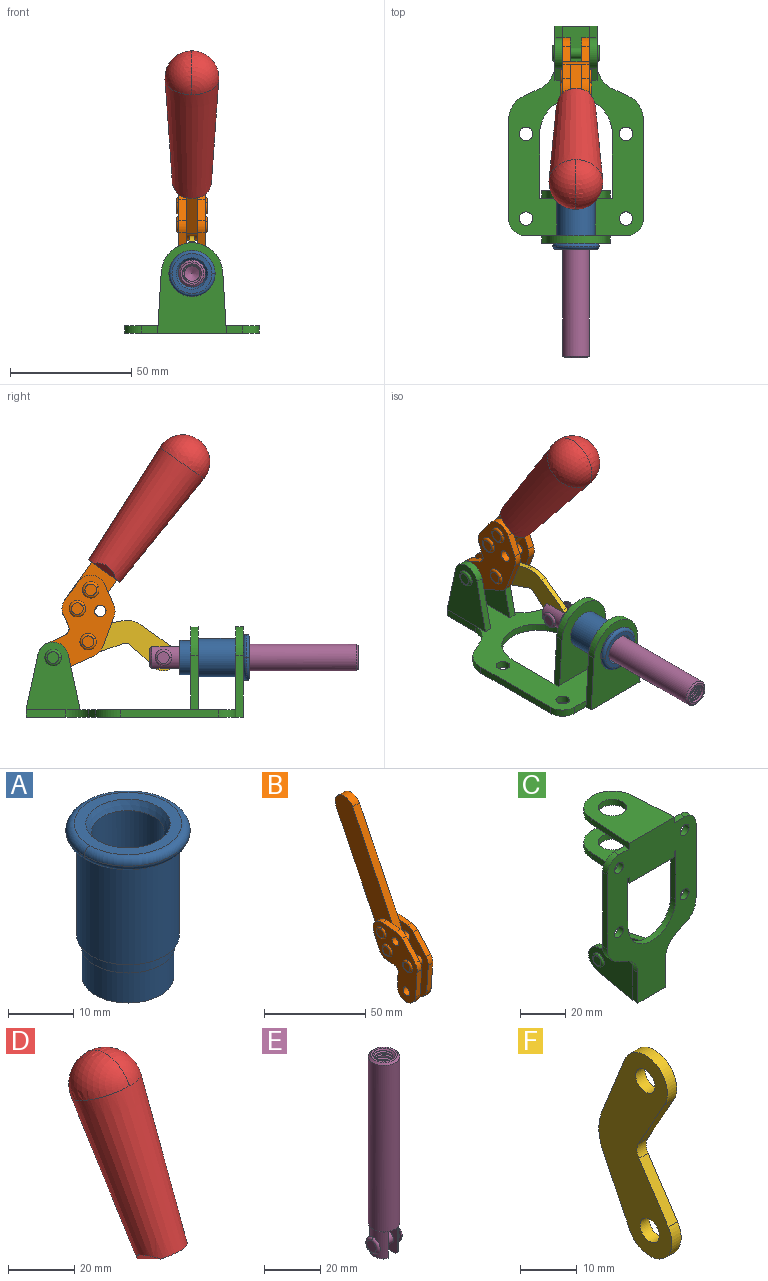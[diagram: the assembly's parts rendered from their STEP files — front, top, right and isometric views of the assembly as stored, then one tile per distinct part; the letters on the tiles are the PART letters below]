
ASSEMBLY  parts=6 mates=6
PART A: 15 faces, bbox 20.6x20.6x28.7 mm
  f0: torus R=8.26mm, axis (0,0,1), area 56.8mm2, adj f1,f10,f12
  f1: torus R=8.26mm, axis (0,0,1), area 56.8mm2, adj f0,f6,f13
  f2: cylinder r=5.59mm len=25.91mm, axis (0,0,1), area 909.6mm2, adj f3,f4
  f3: cone r=6.86mm half-angle=45deg, axis (0,0,-1), area 70.2mm2, adj f2,f14
  f4: cone r=6.47mm half-angle=30deg, axis (0,0,1), area 66.7mm2, adj f2,f13
  f5: cylinder r=7.04mm len=14.07mm, axis (0,0,1), area 252.6mm2, adj f11,f14
  f6: torus R=8.26mm, axis (0,0,1), area 56.8mm2, adj f1,f12,f13
  f7: cylinder r=7.16mm len=14.33mm, axis (0,0,1), area 91.5mm2, adj f9,f11
  f8: cylinder r=7.86mm len=18.42mm, axis (0,0,1), area 909.6mm2, adj f9,f10
  f9: plane 15.72x15.72mm, normal (0,0,-1), area 33mm2, adj f7,f8
  f10: plane 16.51x16.51mm, normal (0,0,-1), area 19.9mm2, adj f0,f8,f12
  f11: plane 14.33x14.33mm, normal (0,0,-1), area 5.7mm2, adj f5,f7
  f12: torus R=8.26mm, axis (0,0,1), area 56.8mm2, adj f0,f6,f10
  f13: plane 16.51x16.51mm, normal (0,0,1), area 82.7mm2, adj f1,f4,f6
  f14: plane 14.07x14.07mm, normal (0,0,-1), area 7.8mm2, adj f3,f5
PART B: 59 faces, bbox 12.9x60.2x99.6 mm
  f0: torus R=2.39mm, axis (-1,0,0), area 14.9mm2, adj f20,f43,f51
  f1: torus R=2.39mm, axis (-1,0,0), area 14.9mm2, adj f19,f42,f51
  f2: torus R=2.39mm, axis (-1,0,0), area 14.9mm2, adj f18,f35,f51
  f3: torus R=2.39mm, axis (-1,0,0), area 14.9mm2, adj f14,f17,f23
  f4: torus R=2.39mm, axis (-1,0,0), area 14.9mm2, adj f13,f16,f23
  f5: torus R=2.39mm, axis (-1,0,0), area 14.9mm2, adj f12,f15,f23
  f6: cylinder r=2.39mm len=4.78mm, axis (1,0,0), area 46.5mm2, adj f48,f50,f51
  f7: cylinder r=2.39mm len=4.78mm, axis (1,0,0), area 46.5mm2, adj f50,f51
  f8: cylinder r=6.35mm len=12.68mm, axis (1,0,0), area 61.8mm2, adj f38,f39,f50,f51
  f9: cylinder r=2.39mm len=4.78mm, axis (-1,0,0), area 70.5mm2, adj f46,f50
  f10: cylinder r=2.39mm len=4.78mm, axis (-1,0,0), area 46.5mm2, adj f23,f45,f46
  f11: cylinder r=2.39mm len=4.78mm, axis (-1,0,0), area 46.5mm2, adj f23,f46
  f12: plane 4.78x4.78mm, normal (1,0,0), area 17.9mm2, adj f5,f15
  f13: plane 4.78x4.78mm, normal (1,0,0), area 17.9mm2, adj f4,f16
  f14: plane 4.78x4.78mm, normal (1,0,0), area 17.9mm2, adj f3,f17
  f15: torus R=2.39mm, axis (-1,0,0), area 14.9mm2, adj f5,f12,f23
  f16: torus R=2.39mm, axis (-1,0,0), area 14.9mm2, adj f4,f13,f23
  f17: torus R=2.39mm, axis (-1,0,0), area 14.9mm2, adj f3,f14,f23
  f18: plane 4.78x4.78mm, normal (-1,0,0), area 17.9mm2, adj f2,f35
  f19: plane 4.78x4.78mm, normal (-1,0,0), area 17.9mm2, adj f1,f42
  f20: plane 4.78x4.78mm, normal (-1,0,0), area 17.9mm2, adj f0,f43
  f21: plane 2.26x0.2mm, normal (1,0,0), area 0.2mm2, adj f31,f44
  f22: plane 2.26x0.2mm, normal (-1,0,0), area 0.2mm2, adj f41,f44
  f23: plane 39.37x30.77mm, normal (1,0,0), area 565.5mm2, adj f3,f4,f5,f10,f11,f15,f16,f17
  f24: cylinder r=6.1mm len=4.15mm, axis (-1,0,0), area 14.7mm2, adj f23,f25,f32,f46
  f25: plane 10.25x9.01mm, normal (0,-0.75,0.66), area 42.3mm2, adj f23,f24,f26,f46
  f26: cylinder r=6.35mm len=4.64mm, axis (-1,0,0), area 15.6mm2, adj f23,f25,f27,f46
  f27: plane 15.84x3.1mm, normal (0,-1,-0.07), area 49.2mm2, adj f23,f26,f28,f46
  f28: cylinder r=6.35mm len=12.68mm, axis (-1,0,0), area 61.8mm2, adj f23,f27,f29,f46
  f29: plane 8.11x3.1mm, normal (0,1,0.07), area 25.2mm2, adj f23,f28,f30,f46
  f30: cylinder r=3.05mm len=3.25mm, axis (-1,0,0), area 14.8mm2, adj f23,f29,f31,f46
  f31: plane 5.99x3.1mm, normal (0,0.07,-1), area 18.6mm2, adj f21,f23,f30,f44,f46
  f32: plane 9.5x3.1mm, normal (0,-0.07,1), area 29.5mm2, adj f23,f24,f33,f46,f47
  f33: cylinder r=6.1mm len=8.63mm, axis (-1,0,0), area 39.1mm2, adj f23,f32,f34,f47
  f34: plane 8.65x3.96mm, normal (0,0.91,-0.42), area 29.5mm2, adj f23,f33,f44,f47
  f35: torus R=2.39mm, axis (-1,0,0), area 14.9mm2, adj f2,f18,f51
  f36: plane 10.25x9.01mm, normal (0,-0.75,0.66), area 42.3mm2, adj f37,f49,f50,f51
  f37: cylinder r=6.35mm len=4.64mm, axis (1,0,0), area 15.6mm2, adj f36,f38,f50,f51
  f38: plane 15.84x3.1mm, normal (0,-1,-0.07), area 49.2mm2, adj f8,f37,f50,f51
  f39: plane 8.11x3.1mm, normal (0,1,0.07), area 25.2mm2, adj f8,f40,f50,f51
  f40: cylinder r=3.05mm len=3.25mm, axis (1,0,0), area 14.8mm2, adj f39,f41,f50,f51
  f41: plane 5.99x3.1mm, normal (0,0.07,-1), area 18.6mm2, adj f22,f40,f44,f50,f51
  f42: torus R=2.39mm, axis (-1,0,0), area 14.9mm2, adj f1,f19,f51
  f43: torus R=2.39mm, axis (-1,0,0), area 14.9mm2, adj f0,f20,f51
  f44: cylinder r=6.35mm len=12.12mm, axis (-1,0,0), area 128.9mm2, adj f21,f22,f23,f31,f34,f41,f46,f47
  f45: plane 2.65x1.35mm, normal (1,0,0), area 1mm2, adj f10,f55
  f46: plane 39.08x20.42mm, normal (-1,0,0), area 412.5mm2, adj f9,f10,f11,f24,f25,f26,f27,f28
  f47: plane 77.62x39.82mm, normal (1,0,0), area 850mm2, adj f32,f33,f34,f44,f53,f54,f55
  f48: plane 2.65x1.35mm, normal (-1,0,0), area 1mm2, adj f6,f55
  f49: cylinder r=6.1mm len=4.15mm, axis (1,0,0), area 14.7mm2, adj f36,f50,f51,f56
  f50: plane 39.08x20.42mm, normal (1,0,0), area 412.5mm2, adj f6,f7,f8,f9,f36,f37,f38,f39
  f51: plane 39.37x30.77mm, normal (-1,0,0), area 565.5mm2, adj f0,f1,f2,f6,f7,f8,f35,f36
  f52: plane 8.65x3.96mm, normal (0,0.91,-0.42), area 29.5mm2, adj f44,f51,f57,f58
  f53: plane 68.49x33.4mm, normal (0,0.9,-0.44), area 358.1mm2, adj f44,f47,f54,f58
  f54: cylinder r=6.35mm len=12.06mm, axis (1,0,0), area 93.7mm2, adj f47,f53,f55,f58
  f55: plane 68.49x33.4mm, normal (0,-0.9,0.44), area 358.1mm2, adj f44,f45,f46,f47,f48,f50,f54,f58
  f56: plane 9.5x3.1mm, normal (0,-0.07,1), area 29.5mm2, adj f49,f50,f51,f57,f58
  f57: cylinder r=6.1mm len=8.63mm, axis (1,0,0), area 39.1mm2, adj f51,f52,f56,f58
  f58: plane 77.62x39.82mm, normal (-1,0,0), area 850mm2, adj f44,f52,f53,f54,f55,f56,f57
PART C: 55 faces, bbox 55.7x37.4x89.8 mm
  f0: torus R=2.41mm, axis (-1,0,0), area 15mm2, adj f11,f15,f25
  f1: torus R=2.41mm, axis (-1,0,0), area 15mm2, adj f10,f12,f22
  f2: cylinder r=2.78mm len=5.56mm, axis (0,-1,0), area 54.2mm2, adj f30,f54
  f3: cylinder r=14.99mm len=29.97mm, axis (0,-1,0), area 145.9mm2, adj f30,f49,f53,f54
  f4: cylinder r=2.78mm len=5.56mm, axis (0,-1,0), area 54.2mm2, adj f30,f54
  f5: cylinder r=2.78mm len=5.56mm, axis (0,-1,0), area 54.2mm2, adj f30,f54
  f6: cylinder r=2.78mm len=5.56mm, axis (0,-1,0), area 54.2mm2, adj f30,f54
  f7: cylinder r=6.35mm len=12.7mm, axis (0,0,1), area 123.6mm2, adj f27,f51
  f8: cylinder r=6.35mm len=12.7mm, axis (0,0,-1), area 124.7mm2, adj f21,f35
  f9: cylinder r=2.41mm len=11.18mm, axis (-1,0,0), area 169.4mm2, adj f16,f19
  f10: plane 4.83x4.83mm, normal (1,0,0), area 18.3mm2, adj f1,f12
  f11: plane 4.83x4.83mm, normal (-1,0,0), area 18.3mm2, adj f0,f15
  f12: torus R=2.41mm, axis (-1,0,0), area 15mm2, adj f1,f10,f22
  f13: cylinder r=6.35mm len=12.41mm, axis (1,0,0), area 53.4mm2, adj f18,f19,f22,f23
  f14: cylinder r=6.35mm len=12.41mm, axis (-1,0,0), area 53.4mm2, adj f16,f17,f24,f25
  f15: torus R=2.41mm, axis (-1,0,0), area 15mm2, adj f0,f11,f25
  f16: plane 27.86x22.35mm, normal (1,0,0), area 425.4mm2, adj f9,f14,f17,f24,f30
  f17: plane 22.86x4.97mm, normal (0,0.21,0.98), area 72.5mm2, adj f14,f16,f25,f30
  f18: plane 22.86x4.97mm, normal (0,0.21,0.98), area 72.5mm2, adj f13,f19,f22,f30
  f19: plane 27.86x22.35mm, normal (-1,0,0), area 425.4mm2, adj f9,f13,f18,f23,f30
  f20: cylinder r=12.7mm len=25.35mm, axis (0,0,-1), area 119.8mm2, adj f21,f34,f35,f36
  f21: plane 34.21x28.07mm, normal (0,0,-1), area 702.4mm2, adj f8,f20,f30,f34,f36
  f22: plane 27.96x22.45mm, normal (1,0,0), area 407.2mm2, adj f1,f12,f13,f18,f23,f30,f42,f43
  f23: plane 22.86x4.97mm, normal (0,0.21,-0.98), area 72.5mm2, adj f13,f19,f22,f44
  f24: plane 22.86x4.97mm, normal (0,0.21,-0.98), area 72.5mm2, adj f14,f16,f25,f44
  f25: plane 27.86x22.35mm, normal (-1,0,0), area 407.1mm2, adj f0,f14,f15,f17,f24,f30,f45,f46
  f26: plane 3.1x0.95mm, normal (0,0,-1), area 2.7mm2, adj f30,f49,f50,f54
  f27: plane 34.21x28.07mm, normal (0,0,1), area 702.4mm2, adj f7,f28,f30,f50,f52
  f28: cylinder r=12.7mm len=25.35mm, axis (0,0,1), area 118.8mm2, adj f27,f50,f51,f52
  f29: plane 3.1x0.95mm, normal (0,0,-1), area 2.7mm2, adj f30,f52,f53,f54
  f30: plane 86.54x55.63mm, normal (0,1,0), area 2362.9mm2, adj f2,f3,f4,f5,f6,f16,f17,f18
  f31: plane 40.56x3.1mm, normal (-1,0,0), area 125.7mm2, adj f30,f32,f48,f54
  f32: cylinder r=7.11mm len=7.11mm, axis (0,-1,0), area 34.6mm2, adj f30,f31,f33,f54
  f33: plane 6.67x3.1mm, normal (0,0,1), area 20.4mm2, adj f30,f32,f34,f54
  f34: plane 25.39x3.13mm, normal (-1,0.06,0), area 79.5mm2, adj f20,f21,f33,f35,f54
  f35: plane 37.31x28.45mm, normal (0,0,1), area 789.9mm2, adj f8,f20,f34,f36,f54
  f36: plane 25.39x3.13mm, normal (1,0.06,0), area 79.5mm2, adj f20,f21,f35,f37,f54
  f37: plane 6.67x3.1mm, normal (0,0,1), area 20.4mm2, adj f30,f36,f38,f54
  f38: cylinder r=7.11mm len=7.11mm, axis (0,-1,0), area 34.6mm2, adj f30,f37,f39,f54
  f39: plane 40.56x3.1mm, normal (1,0,0), area 125.7mm2, adj f30,f38,f40,f54
  f40: cylinder r=11.18mm len=10.16mm, axis (0,-1,0), area 39.5mm2, adj f30,f39,f41,f54
  f41: plane 6.09x3.1mm, normal (0.42,0,-0.91), area 20.8mm2, adj f30,f40,f42,f54
  f42: cylinder r=11.18mm len=9.41mm, axis (0,-1,0), area 37.2mm2, adj f22,f30,f41,f43,f54
  f43: plane 16.5x3.1mm, normal (1,0,0), area 51.1mm2, adj f22,f42,f44,f54
  f44: plane 17.37x3.1mm, normal (0,0,-1), area 53.8mm2, adj f23,f24,f30,f43,f45,f54
  f45: plane 16.5x3.1mm, normal (-1,0,0), area 51.1mm2, adj f25,f44,f46,f54
  f46: cylinder r=11.18mm len=9.41mm, axis (0,-1,0), area 37.2mm2, adj f25,f30,f45,f47,f54
  f47: plane 6.09x3.1mm, normal (-0.42,0,-0.91), area 20.8mm2, adj f30,f46,f48,f54
  f48: cylinder r=11.18mm len=10.16mm, axis (0,-1,0), area 39.5mm2, adj f30,f31,f47,f54
  f49: plane 26.54x3.1mm, normal (-1,0,0), area 82.3mm2, adj f3,f26,f30,f54
  f50: plane 25.39x3.1mm, normal (1,0.06,0), area 78.8mm2, adj f26,f27,f28,f51,f54
  f51: plane 37.31x28.45mm, normal (0,0,-1), area 789.9mm2, adj f7,f28,f50,f52,f54
  f52: plane 25.39x3.1mm, normal (-1,0.06,0), area 78.8mm2, adj f27,f28,f29,f51,f54
  f53: plane 26.54x3.1mm, normal (1,0,0), area 82.3mm2, adj f3,f29,f30,f54
  f54: plane 89.66x55.63mm, normal (0,-1,0), area 2678.5mm2, adj f2,f3,f4,f5,f6,f26,f29,f31
PART D: 11 faces, bbox 22.3x42.6x64.5 mm
  f0: sphere r=11.13mm, area 411.4mm2, adj f1,f8
  f1: cone r=11.11mm half-angle=3.3deg, axis (0,0.44,0.9), area 3251.8mm2, adj f0,f7,f8,f9,f10
  f2: cylinder r=6.16mm len=11.7mm, axis (1,0,0), area 89.5mm2, adj f3,f4,f5,f6
  f3: plane 60.23x36.75mm, normal (-1,0,0), area 763.6mm2, adj f2,f4,f6,f10
  f4: plane 51.37x25.05mm, normal (0,0.9,-0.44), area 264.2mm2, adj f2,f3,f5,f10
  f5: plane 60.23x36.75mm, normal (1,0,0), area 763.6mm2, adj f2,f4,f6,f10
  f6: plane 51.37x25.05mm, normal (0,-0.9,0.44), area 264.2mm2, adj f2,f3,f5,f10
  f7: plane 9.95x5.95mm, normal (0.71,-0.31,-0.64), area 25.8mm2, adj f1,f10
  f8: sphere r=11.13mm, area 411.4mm2, adj f0,f1
  f9: plane 9.95x5.95mm, normal (-0.71,-0.31,-0.64), area 25.8mm2, adj f1,f10
  f10: plane 14.27x11.38mm, normal (0,-0.44,-0.9), area 106.7mm2, adj f1,f3,f4,f5,f6,f7,f9
PART E: 48 faces, bbox 12.6x11.1x86.1 mm
  f0: torus R=2.41mm, axis (-1,0,0), area 15mm2, adj f30,f32,f34
  f1: torus R=2.41mm, axis (-1,0,0), area 15mm2, adj f29,f31,f33
  f2: cylinder r=5.54mm len=72.39mm, axis (0,0,1), area 2518.5mm2, adj f3,f4,f42,f43
  f3: cone r=5.54mm half-angle=45deg, axis (0,0,1), area 7.6mm2, adj f2,f5,f41
  f4: cone r=5.54mm half-angle=45deg, axis (0,0,-1), area 34.9mm2, adj f2,f39
  f5: cylinder r=5.08mm len=11.48mm, axis (0,0,1), area 108.3mm2, adj f3,f7,f8,f41
  f6: cylinder r=2.41mm len=4.83mm, axis (-1,0,0), area 71.2mm2, adj f40,f41
  f7: cylinder r=2.41mm len=4.83mm, axis (-1,0,0), area 7.6mm2, adj f5,f34
  f8: cone r=5.08mm half-angle=45deg, axis (0,0,1), area 10.6mm2, adj f5,f37,f41
  f9: cone r=3.98mm half-angle=45deg, axis (0,0,1), area 17.6mm2, adj f27,f39,f45,f46,f47
  f10: cylinder r=2.41mm len=4.83mm, axis (-1,0,0), area 7.6mm2, adj f33,f38
  f11: cylinder r=3.2mm len=6.4mm, axis (0,0,1), area 78.4mm2, adj f12,f28,f44,f45,f47
  f12: cylinder r=3.2mm len=6.4mm, axis (0,0,1), area 10.5mm2, adj f11,f13,f45,f47
  f13: cylinder r=3.2mm len=6.4mm, axis (0,0,1), area 10.5mm2, adj f12,f14,f45,f47
  f14: cylinder r=3.2mm len=6.4mm, axis (0,0,1), area 10.5mm2, adj f13,f15,f45,f47
  f15: cylinder r=3.2mm len=6.4mm, axis (0,0,1), area 10.5mm2, adj f14,f16,f45,f47
  f16: cylinder r=3.2mm len=6.4mm, axis (0,0,1), area 10.5mm2, adj f15,f17,f45,f47
  f17: cylinder r=3.2mm len=6.4mm, axis (0,0,1), area 10.5mm2, adj f16,f18,f45,f47
  f18: cylinder r=3.2mm len=6.4mm, axis (0,0,1), area 10.5mm2, adj f17,f19,f45,f47
  f19: cylinder r=3.2mm len=6.4mm, axis (0,0,1), area 10.5mm2, adj f18,f20,f45,f47
  f20: cylinder r=3.2mm len=6.4mm, axis (0,0,1), area 10.5mm2, adj f19,f21,f45,f47
  f21: cylinder r=3.2mm len=6.4mm, axis (0,0,1), area 10.5mm2, adj f20,f22,f45,f47
  f22: cylinder r=3.2mm len=6.4mm, axis (0,0,1), area 10.5mm2, adj f21,f23,f45,f47
  f23: cylinder r=3.2mm len=6.4mm, axis (0,0,1), area 10.5mm2, adj f22,f24,f45,f47
  f24: cylinder r=3.2mm len=6.4mm, axis (0,0,1), area 10.5mm2, adj f23,f25,f45,f47
  f25: cylinder r=3.2mm len=6.4mm, axis (0,0,1), area 10.5mm2, adj f24,f26,f45,f47
  f26: cylinder r=3.2mm len=6.4mm, axis (0,0,1), area 10.5mm2, adj f25,f27,f45,f47
  f27: cylinder r=3.2mm len=6.4mm, axis (0,0,1), area 7.4mm2, adj f9,f26,f45,f47
  f28: cone r=3.2mm half-angle=60deg, axis (0,0,1), area 37.2mm2, adj f11
  f29: plane 4.83x4.83mm, normal (-1,0,0), area 18.3mm2, adj f1,f31
  f30: plane 4.83x4.83mm, normal (1,0,0), area 18.3mm2, adj f0,f32
  f31: torus R=2.41mm, axis (-1,0,0), area 15mm2, adj f1,f29,f33
  f32: torus R=2.41mm, axis (-1,0,0), area 15mm2, adj f0,f30,f34
  f33: plane 6.83x6.83mm, normal (1,0,0), area 18.3mm2, adj f1,f10,f31
  f34: plane 6.83x6.83mm, normal (-1,0,0), area 18.3mm2, adj f0,f7,f32
  f35: cone r=5.08mm half-angle=45deg, axis (0,0,1), area 10.6mm2, adj f36,f38,f40
  f36: plane 7.25x1.97mm, normal (0,0,-1), area 10mm2, adj f35,f40
  f37: plane 7.25x1.97mm, normal (0,0,-1), area 10mm2, adj f8,f41
  f38: cylinder r=5.08mm len=11.48mm, axis (0,0,1), area 108.3mm2, adj f10,f35,f40,f42
  f39: plane 9.55x9.55mm, normal (0,0,1), area 22mm2, adj f4,f9
  f40: plane 12.76x10.09mm, normal (1,0,0), area 95.7mm2, adj f6,f35,f36,f38,f42,f43
  f41: plane 12.76x10.09mm, normal (-1,0,0), area 95.7mm2, adj f3,f5,f6,f8,f37,f43
  f42: cone r=5.54mm half-angle=45deg, axis (0,0,1), area 7.6mm2, adj f2,f38,f40
  f43: plane 11.07x4.7mm, normal (0,0,-1), area 50.4mm2, adj f2,f40,f41
  f44: plane 0.89x0.62mm, normal (-1,0,0), area 0.3mm2, adj f11,f45,f46,f47
  f45: bspline ~24.8x7.63mm, area 266.6mm2, adj f9,f11,f12,f13,f14,f15,f16,f17
  f46: bspline ~24.87x7.63mm, area 73.6mm2, adj f9,f44,f45,f47
  f47: bspline ~24.98x7.63mm, area 272.5mm2, adj f9,f11,f12,f13,f14,f15,f16,f17
PART F: 12 faces, bbox 2.3x18.2x42.8 mm
  f0: cylinder r=2.4mm len=4.8mm, axis (1,0,0), area 34.9mm2, adj f4,f11
  f1: cylinder r=10.41mm len=8.47mm, axis (1,0,0), area 20.2mm2, adj f4,f9,f10,f11
  f2: cylinder r=3.05mm len=3.16mm, axis (1,0,0), area 7.7mm2, adj f4,f6,f7,f11
  f3: cylinder r=2.4mm len=4.8mm, axis (1,0,0), area 34.9mm2, adj f4,f11
  f4: plane 42.81x18.23mm, normal (-1,0,0), area 414.1mm2, adj f0,f1,f2,f3,f5,f6,f7,f8
  f5: cylinder r=5.54mm len=10.67mm, axis (1,0,0), area 41.8mm2, adj f4,f6,f10,f11
  f6: plane 11.66x6.53mm, normal (0,-0.87,-0.49), area 30.9mm2, adj f2,f4,f5,f11
  f7: plane 11.17x7.33mm, normal (0,-0.84,0.55), area 30.9mm2, adj f2,f4,f8,f11
  f8: cylinder r=5.54mm len=10.51mm, axis (1,0,0), area 41.8mm2, adj f4,f7,f9,f11
  f9: plane 13.67x6.67mm, normal (0,0.9,-0.44), area 35.1mm2, adj f1,f4,f8,f11
  f10: plane 14.1x5.7mm, normal (0,0.93,0.37), area 35.1mm2, adj f1,f4,f5,f11
  f11: plane 42.81x18.23mm, normal (1,0,0), area 414.1mm2, adj f0,f1,f2,f3,f5,f6,f7,f8
PLACE A rot(axis=(1,0,0),90deg) t=(0,9.14,0)mm
PLACE B rot(axis=(1,0,0),61.7deg) t=(0,1.31,18.16)mm
PLACE C rot(axis=(1,0,0),90deg) t=(0,9.14,0)mm fixed
PLACE D rot(axis=(1,0,0),61.7deg) t=(-0.04,1.31,18.16)mm
PLACE E rot(axis=(1,0,0),90deg) t=(0,11.17,0)mm
PLACE F rot(axis=(1,0,0),103.9deg) t=(0,16.62,4.43)mm
MATE revolute B.f4 <-> F.f3  axis (-1,0,0) through (0,26.77,31.15)mm
MATE slider E.f2 <-> C.f7  axis (0,-1,0) through (0,-47.61,24.61)mm
MATE fastened D.f2 <-> B.f54  axis (1,0,0) through (-2.35,-13.23,106.68)mm
MATE revolute C.f0 <-> B.f7  axis (-1,0,0) through (0,41.23,24.61)mm
MATE fastened A.f0 <-> C.f7  axis (0,1,0) through (0,-37.25,24.61)mm
MATE revolute E.f6 <-> F.f5  axis (-1,0,0) through (0,-4.3,24.61)mm
